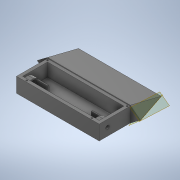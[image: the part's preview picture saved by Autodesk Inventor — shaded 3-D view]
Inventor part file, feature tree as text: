
AUTODESK INVENTOR PART (.ipt)
format: ipt  version: 2020 (Build 240168000, 168)  size: 376,320 bytes
history: native  units: in
note: dims shown in document units (in); Inventor stores cm internally (conversion verified against a paired STEP export)
features: extrude x11, sketch x9, projected_geometry x7, plane x5, mirror x2
ambient origin geometry x8: Origin, YZ Plane, XZ Plane, XY Plane, X Axis, Y Axis, Z Axis, Center Point
bodies: Solid1 (feature_tree)
feature tree (34):
  extrude  "Extrusion1"  Depth=2.3622in
  extrude  "Extrusion2"  Depth=0.1181in TaperAngle=0.0deg
  extrude  "Extrusion5"  Depth=0.0787in
  extrude  "Extrusion6"  Depth=0.7874in TaperAngle=0.0deg
  extrude  "Extrusion7"  Depth=0.2756in
  mirror  "Mirror2"
  extrude  "Extrusion18"  Depth=0.7874in
  plane  "Work Plane9"
  extrude  "Extrusion19"  Depth=1.8898in
  plane  "Work Plane4"
  extrude  "Extrusion20"  Depth=0.6299in
  plane  "Work Plane5"
  extrude  "Extrusion21"  Depth=0.3937in
  mirror  "Mirror10"
  extrude  "Extrusion22"  Depth=0.4724in
  extrude  "Extrusion23"  Depth=0.2362in
  sketch  "Sketch2"  dims[d0=6.2992in d1=2.3622in]
  projected_geometry  "Projected Loop1"
  sketch  "Sketch7"  dims[d2=0.1181in d3=0.0in d5=0.9449in d6=0.0in]
  sketch  "Sketch8"  dims[d18=0.5906in d20=0.0787in]
  projected_geometry  "Projected Loop5"
  sketch  "Sketch9"  dims[d21=0.4429in d22=0.0in d25=0.7874in d26=0.0in]
  projected_geometry  "Projected Loop6"
  sketch  "Sketch23"  dims[d27=0.2756in d28=0.5906in]
  sketch  "Sketch24"  dims[d30=0.4626in d31=0.0in d32=0.7874in]
  sketch  "Sketch25"  dims[d36=5.8268in d37=1.8898in]
  plane  "Work Plane7"
  plane  "Work Plane8"
  projected_geometry  "Projected Loop11"
  projected_geometry  "Projected Loop12"
  sketch  "Sketch26"  dims[d40=0.7874in d41=0.6299in]
  projected_geometry  "Projected Loop13"
  sketch  "Sketch27"  dims[d55=0.6102in d62=0.3937in d63=0.4724in d64=0.2362in d95=0.2362in d96=0.0in d97=0.7874in d98=2.3622in d99=0.0in d100=2.3622in d101=0.0in d102=2.3622in d103=0.0in d104=1.1811in d105=0.5906in d106=2.3622in d108=0.5906in d109=0.0556in d110=0.0in d111=0.1181in d112=0.1181in d113=0.1181in d114=0.1142in d115=0.6693in d116=0.1142in d117=0.2756in d118=0.0in d50=0.0197in d51=0.0344in d52=0.0197in d53=0.0344in d73=0.0197in d74=0.0344in d75=0.0197in d76=0.0344in]
  projected_geometry  "Projected Loop14"
